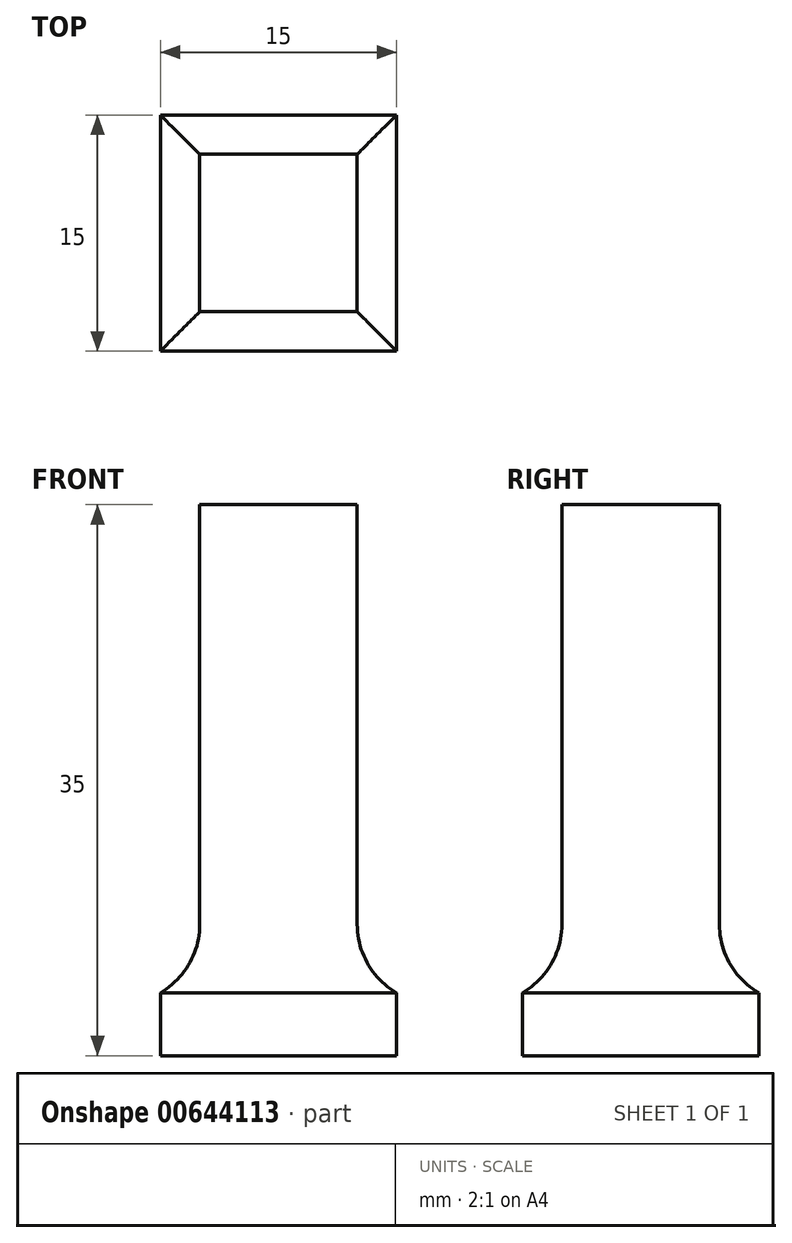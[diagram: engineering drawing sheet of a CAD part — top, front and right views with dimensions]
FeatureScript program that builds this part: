
annotation { "Feature Type Name" : "Feature", "Feature Type Description" : "" }
export const myFeature = defineFeature(function(context is Context, id is Id, definition is map)
    precondition{}
    {
        {
            var Q0;
            Q0=qCreatedBy(makeId("Top.planeOp"),FACE);
            var sketch = newSketch(context, id + "F0", { "sketchPlane" : qUnion([Q0])});
            skLineSegment(sketch, "E0.bottom", {"start": v(-5, 5) * mm, "end": v(5, 5) * mm});
            skLineSegment(sketch, "E0.top", {"start": v(-5, -5) * mm, "end": v(5, -5) * mm});
            skLineSegment(sketch, "E0.left", {"start": v(-5, 5) * mm, "end": v(-5, -5) * mm});
            skLineSegment(sketch, "E0.right", {"start": v(5, 5) * mm, "end": v(5, -5) * mm});
            skSolve(sketch);
        }
        {
            var Q0;
            Q0 = qSketchRegion(id + "F0", true);
            extrude(context, id + "F1", {"entities" : qUnion([Q0]), "depth" : 35 * mm, "offsetDistance" : 25 * mm});
        }
        {
            var Q0;
            Q0=qCreatedBy(makeId("Top.planeOp"),FACE);
            var sketch = newSketch(context, id + "F2", { "sketchPlane" : qUnion([Q0])});
            skLineSegment(sketch, "E1.bottom", {"start": v(-7.5, 7.5) * mm, "end": v(7.5, 7.5) * mm});
            skLineSegment(sketch, "E1.top", {"start": v(-7.5, -7.5) * mm, "end": v(7.5, -7.5) * mm});
            skLineSegment(sketch, "E1.left", {"start": v(-7.5, 7.5) * mm, "end": v(-7.5, -7.5) * mm});
            skLineSegment(sketch, "E1.right", {"start": v(7.5, 7.5) * mm, "end": v(7.5, -7.5) * mm});
            skSolve(sketch);
        }
        {
            var Q0;
            Q0 = qSketchRegion(id + "F2", true);
            extrude(context, id + "F3", {"entities" : qUnion([Q0]), "operationType" : NewBodyOperationType.ADD, "depth" : 4 * mm, "offsetDistance" : 25 * mm});
        }
        {
            var Q0;
            Q0=makeQuery(id+"F3.boolean.opBoolean","INTERSECT",EDGE,{"derivedFrom":[makeQuery(id+"F1.opExtrude","SWEPT_FACE",FACE,{"disambiguationData":[OSD([sQuery(id+"F0.wireOp",EDGE,"E0.left")])]}),makeQuery(id+"F3.opExtrude","CAP_FACE",FACE,{"disambiguationData":[OSD([sQuery(id+"F2.wireOp",EDGE,"E1.bottom"),sQuery(id+"F2.wireOp",EDGE,"E1.top"),sQuery(id+"F2.wireOp",EDGE,"E1.left"),sQuery(id+"F2.wireOp",EDGE,"E1.right")])],"isStart":false})]});
            var Q1;
            Q1=makeQuery(id+"F3.boolean.opBoolean","INTERSECT",EDGE,{"derivedFrom":[makeQuery(id+"F1.opExtrude","SWEPT_FACE",FACE,{"disambiguationData":[OSD([sQuery(id+"F0.wireOp",EDGE,"E0.bottom")])]}),makeQuery(id+"F3.opExtrude","CAP_FACE",FACE,{"disambiguationData":[OSD([sQuery(id+"F2.wireOp",EDGE,"E1.bottom"),sQuery(id+"F2.wireOp",EDGE,"E1.top"),sQuery(id+"F2.wireOp",EDGE,"E1.left"),sQuery(id+"F2.wireOp",EDGE,"E1.right")])],"isStart":false})]});
            var Q2;
            Q2=makeQuery(id+"F3.boolean.opBoolean","INTERSECT",EDGE,{"derivedFrom":[makeQuery(id+"F1.opExtrude","SWEPT_FACE",FACE,{"disambiguationData":[OSD([sQuery(id+"F0.wireOp",EDGE,"E0.right")])]}),makeQuery(id+"F3.opExtrude","CAP_FACE",FACE,{"disambiguationData":[OSD([sQuery(id+"F2.wireOp",EDGE,"E1.bottom"),sQuery(id+"F2.wireOp",EDGE,"E1.top"),sQuery(id+"F2.wireOp",EDGE,"E1.left"),sQuery(id+"F2.wireOp",EDGE,"E1.right")])],"isStart":false})]});
            var Q3;
            Q3=makeQuery(id+"F3.boolean.opBoolean","INTERSECT",EDGE,{"derivedFrom":[makeQuery(id+"F1.opExtrude","SWEPT_FACE",FACE,{"disambiguationData":[OSD([sQuery(id+"F0.wireOp",EDGE,"E0.top")])]}),makeQuery(id+"F3.opExtrude","CAP_FACE",FACE,{"disambiguationData":[OSD([sQuery(id+"F2.wireOp",EDGE,"E1.bottom"),sQuery(id+"F2.wireOp",EDGE,"E1.top"),sQuery(id+"F2.wireOp",EDGE,"E1.left"),sQuery(id+"F2.wireOp",EDGE,"E1.right")])],"isStart":false})]});
            fillet(context, id + "F4", {"entities" : qUnion([Q0, Q1, Q2, Q3]), "radius" : 5 * mm, "tangentPropagation" : true, "allowEdgeOverflow" : false});
        }
    });
